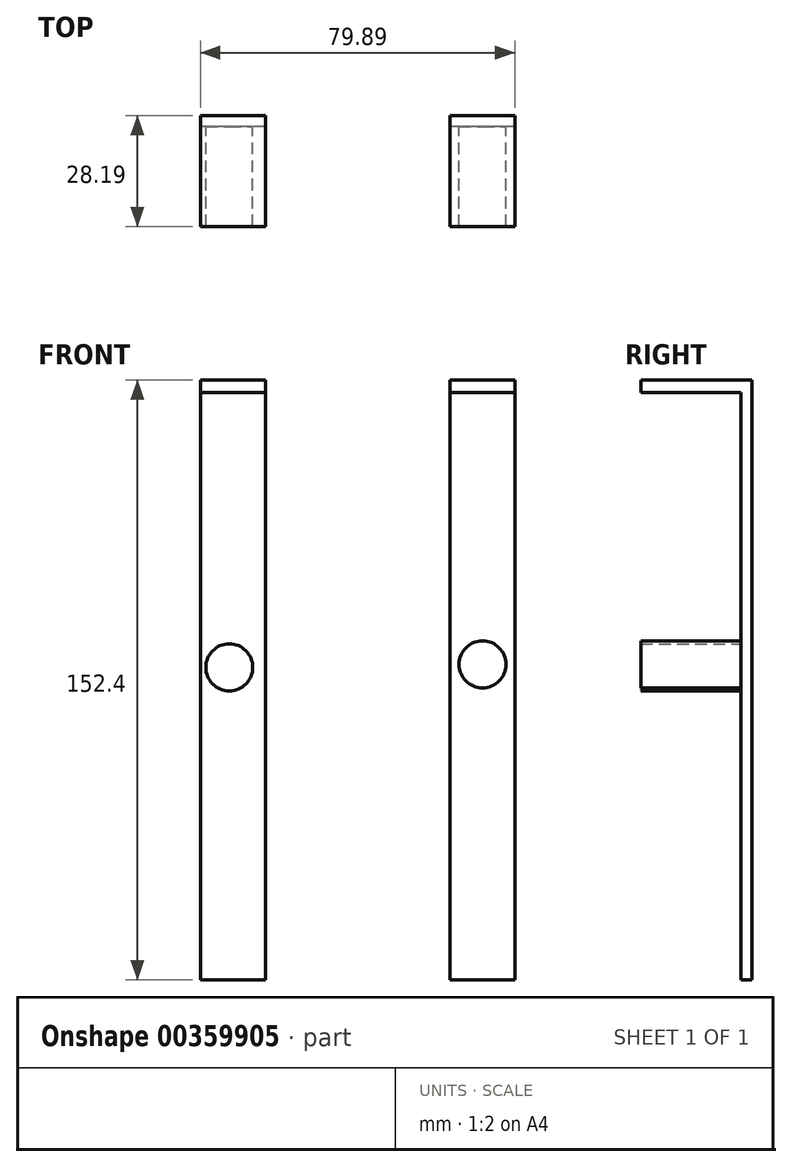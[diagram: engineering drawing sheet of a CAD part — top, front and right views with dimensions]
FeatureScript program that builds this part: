
annotation { "Feature Type Name" : "Feature", "Feature Type Description" : "" }
export const myFeature = defineFeature(function(context is Context, id is Id, definition is map)
    precondition{}
    {
        {
            var Q0;
            Q0=qCreatedBy(makeId("Front.planeOp"),FACE);
            var sketch = newSketch(context, id + "F0", { "sketchPlane" : qUnion([Q0])});
            skLineSegment(sketch, "E0.bottom", {"start": v(-63.38, 88.13) * mm, "end": v(-46.87, 88.13) * mm});
            skLineSegment(sketch, "E0.top", {"start": v(-63.38, -64.27) * mm, "end": v(-46.87, -64.27) * mm});
            skLineSegment(sketch, "E0.left", {"start": v(-63.38, 88.13) * mm, "end": v(-63.38, -64.27) * mm});
            skLineSegment(sketch, "E0.right", {"start": v(-46.87, 88.13) * mm, "end": v(-46.87, -64.27) * mm});
            skLineSegment(sketch, "E1.bottom", {"start": v(16.5, 88.13) * mm, "end": v(0, 88.13) * mm});
            skLineSegment(sketch, "E1.top", {"start": v(16.51, -64.27) * mm, "end": v(0, -64.27) * mm});
            skLineSegment(sketch, "E1.left", {"start": v(16.5, 88.13) * mm, "end": v(16.51, -64.27) * mm});
            skLineSegment(sketch, "E1.right", {"start": v(0, 88.13) * mm, "end": v(0, -64.27) * mm});
            skSolve(sketch);
        }
        {
            var Q0;
            Q0 = qSketchRegion(id + "F0", true);
            extrude(context, id + "F1", {"entities" : qUnion([Q0]), "depth" : 2.8 * mm});
        }
        {
            var Q0;
            Q0=makeQuery(id+"F1.opExtrude","CAP_FACE",FACE,{"disambiguationData":[OSD([sQuery(id+"F0.wireOp",EDGE,"E0.bottom"),sQuery(id+"F0.wireOp",EDGE,"E0.top"),sQuery(id+"F0.wireOp",EDGE,"E0.left"),sQuery(id+"F0.wireOp",EDGE,"E0.right")])],"isStart":false});
            var sketch = newSketch(context, id + "F2", { "sketchPlane" : qUnion([Q0])});
            skLineSegment(sketch, "E2", {"start": v(-63.38, 88.13) * mm, "end": v(-46.87, 88.13) * mm});
            skLineSegment(sketch, "E3", {"start": v(-46.87, 88.13) * mm, "end": v(-46.87, 85) * mm});
            skLineSegment(sketch, "E4", {"start": v(-46.87, 85) * mm, "end": v(-63.38, 85) * mm});
            skLineSegment(sketch, "E5", {"start": v(-63.38, 85) * mm, "end": v(-63.38, 88.13) * mm});
            skSolve(sketch);
        }
        {
            var Q0;
            Q0 = qSketchRegion(id + "F2", true);
            extrude(context, id + "F3", {"entities" : qUnion([Q0]), "operationType" : NewBodyOperationType.ADD, "depth" : 25.4 * mm});
        }
        {
            var Q0;
            Q0=makeQuery(id+"F1.opExtrude","CAP_FACE",FACE,{"disambiguationData":[OSD([sQuery(id+"F0.wireOp",EDGE,"E1.bottom"),sQuery(id+"F0.wireOp",EDGE,"E1.top"),sQuery(id+"F0.wireOp",EDGE,"E1.left"),sQuery(id+"F0.wireOp",EDGE,"E1.right")])],"isStart":false});
            var sketch = newSketch(context, id + "F4", { "sketchPlane" : qUnion([Q0])});
            skLineSegment(sketch, "E6", {"start": v(0, 88.13) * mm, "end": v(16.5, 88.13) * mm});
            skLineSegment(sketch, "E7", {"start": v(16.5, 88.13) * mm, "end": v(16.5, 84.99) * mm});
            skLineSegment(sketch, "E8", {"start": v(16.5, 84.99) * mm, "end": v(0, 84.99) * mm});
            skLineSegment(sketch, "E9", {"start": v(0, 84.99) * mm, "end": v(0, 88.13) * mm});
            skSolve(sketch);
        }
        {
            var Q0;
            Q0 = qSketchRegion(id + "F4", true);
            extrude(context, id + "F5", {"entities" : qUnion([Q0]), "operationType" : NewBodyOperationType.ADD, "depth" : 25.4 * mm});
        }
        {
            var Q0;
            Q0=makeQuery(id+"F1.opExtrude","CAP_FACE",FACE,{"disambiguationData":[OSD([sQuery(id+"F0.wireOp",EDGE,"E0.bottom"),sQuery(id+"F0.wireOp",EDGE,"E0.top"),sQuery(id+"F0.wireOp",EDGE,"E0.left"),sQuery(id+"F0.wireOp",EDGE,"E0.right")])],"isStart":false});
            var sketch = newSketch(context, id + "F6", { "sketchPlane" : qUnion([Q0])});
            skCircle(sketch, "E10", {"center": v(-56.05, 15.13) * mm, "radius": 5.97 * mm});
            skSolve(sketch);
        }
        {
            var Q0;
            Q0 = qSketchRegion(id + "F6", true);
            extrude(context, id + "F7", {"entities" : qUnion([Q0]), "operationType" : NewBodyOperationType.ADD, "depth" : 25.4 * mm});
        }
        {
            var Q0;
            Q0=makeQuery(id+"F1.opExtrude","CAP_FACE",FACE,{"disambiguationData":[OSD([sQuery(id+"F0.wireOp",EDGE,"E1.bottom"),sQuery(id+"F0.wireOp",EDGE,"E1.top"),sQuery(id+"F0.wireOp",EDGE,"E1.left"),sQuery(id+"F0.wireOp",EDGE,"E1.right")])],"isStart":false});
            var sketch = newSketch(context, id + "F8", { "sketchPlane" : qUnion([Q0])});
            skCircle(sketch, "E11", {"center": v(8.3, 15.9) * mm, "radius": 5.97 * mm});
            skSolve(sketch);
        }
        {
            var Q0;
            Q0 = qSketchRegion(id + "F8", true);
            extrude(context, id + "F9", {"entities" : qUnion([Q0]), "operationType" : NewBodyOperationType.ADD, "depth" : 25.4 * mm});
        }
    });
